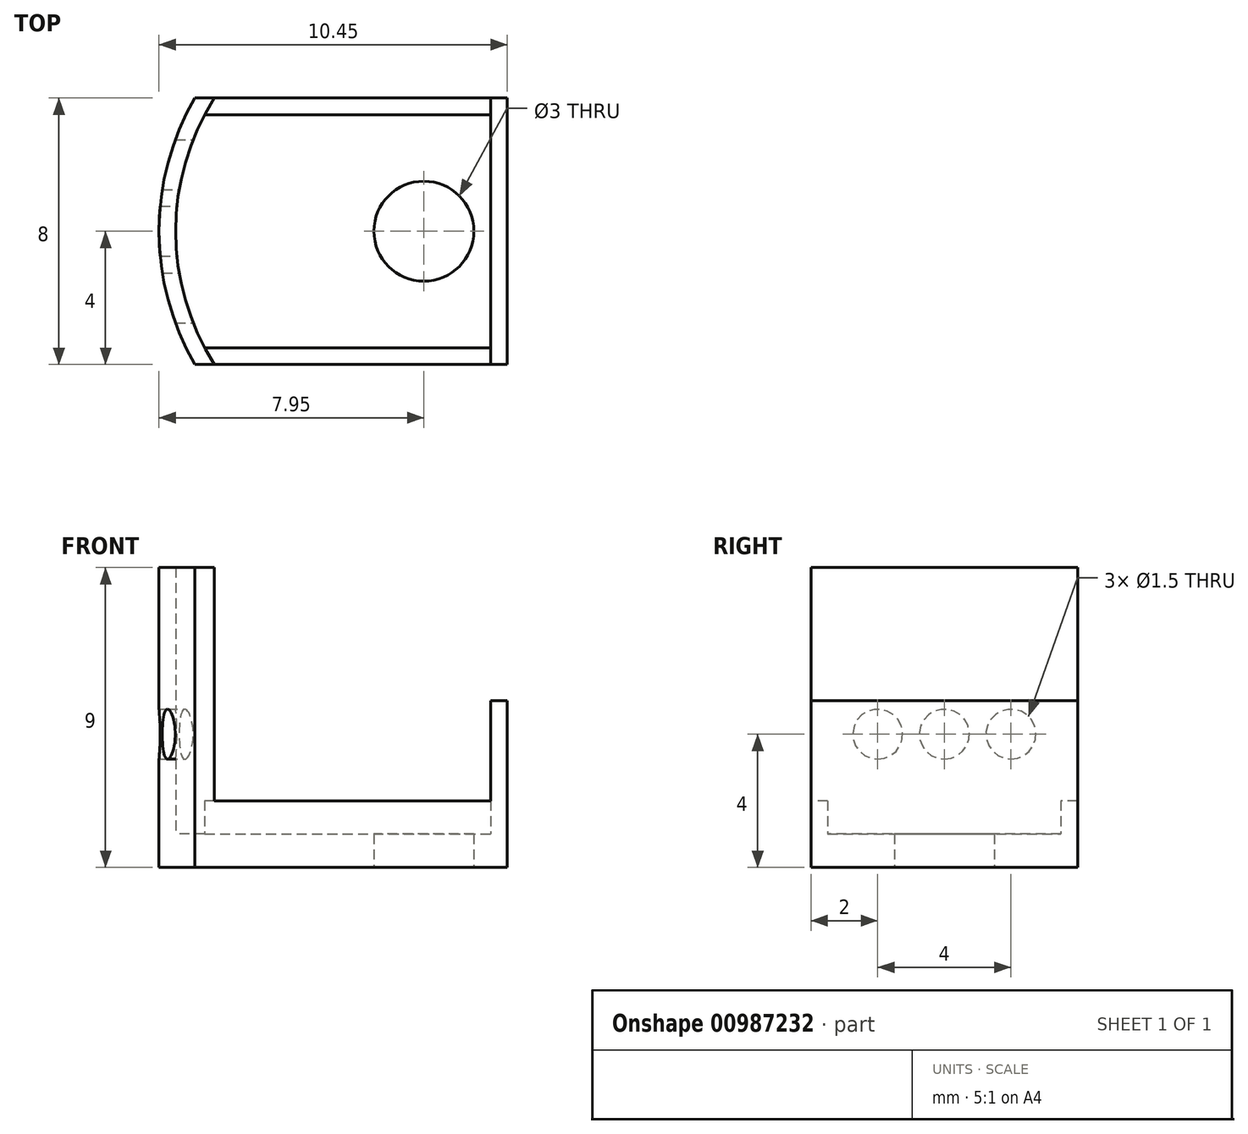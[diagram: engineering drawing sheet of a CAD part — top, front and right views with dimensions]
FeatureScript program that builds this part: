
annotation { "Feature Type Name" : "Feature", "Feature Type Description" : "" }
export const myFeature = defineFeature(function(context is Context, id is Id, definition is map)
    precondition{}
    {
        {
            var Q0;
            Q0=qCreatedBy(makeId("Top.planeOp"),FACE);
            var sketch = newSketch(context, id + "F0", { "sketchPlane" : qUnion([Q0])});
            skLineSegment(sketch, "E0", {"start": v(0, 0) * mm, "end": v(2.5, 0) * mm});
            skCircle(sketch, "E1", {"center": v(0, 0) * mm, "radius": 7.95 * mm});
            skLineSegment(sketch, "E2", {"start": v(2.5, 4) * mm, "end": v(2.5, -4) * mm});
            skLineSegment(sketch, "E3", {"start": v(2.5, 4) * mm, "end": v(-6.87, 4) * mm});
            skCircle(sketch, "E4", {"center": v(0, 0) * mm, "radius": 1.5 * mm});
            skLineSegment(sketch, "E5", {"start": v(2.5, -4) * mm, "end": v(-6.87, -4) * mm});
            skLineSegment(sketch, "E6", {"start": v(2, 4) * mm, "end": v(2, -4) * mm});
            skLineSegment(sketch, "E7", {"start": v(2.5, -3.5) * mm, "end": v(-7.14, -3.5) * mm});
            skLineSegment(sketch, "E8", {"start": v(2.5, 3.5) * mm, "end": v(-7.14, 3.5) * mm});
            skCircle(sketch, "E9", {"center": v(0, 0) * mm, "radius": 7.45 * mm});
            skSolve(sketch);
        }
        {
            var Q0;
            {var subQ5=sQuery(id+"F0.wireOp",EDGE,"E4");Q0=makeQuery(id+"F0.imprint","IMPRINT",FACE,{"disambiguationData":[TD([[makeQuery(id+"F0.imprint","IMPRINT",EDGE,{"derivedFrom":subQ5}),-1.0]])]});}
            var Q1;
            {var subQ0=sQuery(id+"F0.wireOp",EDGE,"E2");var subQ1=sQuery(id+"F0.wireOp",EDGE,"E0");var subQ2=makeQuery(id+"F0.imprint","INTERSECT",VERTEX,{"derivedFrom":[subQ1,subQ0]});Q1=makeQuery(id+"F0.imprint","IMPRINT",FACE,{"disambiguationData":[TD([[makeQuery(id+"F0.imprint","IMPRINT",EDGE,{"disambiguationData":[TD([[subQ2,-1.0]])],"derivedFrom":subQ0}),-1.0]])]});}
            var Q2;
            {var subQ0=sQuery(id+"F0.wireOp",EDGE,"E2");var subQ1=sQuery(id+"F0.wireOp",EDGE,"E0");var subQ2=makeQuery(id+"F0.imprint","INTERSECT",VERTEX,{"derivedFrom":[subQ1,subQ0]});Q2=makeQuery(id+"F0.imprint","IMPRINT",FACE,{"disambiguationData":[TD([[makeQuery(id+"F0.imprint","IMPRINT",EDGE,{"disambiguationData":[TD([[subQ2,1.0]])],"derivedFrom":subQ0}),-1.0]])]});}
            var Q3;
            {var subQ0=sQuery(id+"F0.wireOp",EDGE,"E5");var subQ1=sQuery(id+"F0.wireOp",EDGE,"E1");var subQ2=makeQuery(id+"F0.imprint","INTERSECT",VERTEX,{"derivedFrom":[subQ1,subQ0]});Q3=makeQuery(id+"F0.imprint","IMPRINT",FACE,{"disambiguationData":[TD([[makeQuery(id+"F0.imprint","IMPRINT",EDGE,{"disambiguationData":[TD([[subQ2,1.0]])],"derivedFrom":subQ1}),1.0]])]});}
            var Q4;
            {var subQ0=sQuery(id+"F0.wireOp",EDGE,"E3");var subQ1=sQuery(id+"F0.wireOp",EDGE,"E1");var subQ2=makeQuery(id+"F0.imprint","INTERSECT",VERTEX,{"derivedFrom":[subQ1,subQ0]});Q4=makeQuery(id+"F0.imprint","IMPRINT",FACE,{"disambiguationData":[TD([[makeQuery(id+"F0.imprint","IMPRINT",EDGE,{"disambiguationData":[TD([[subQ2,-1.0]])],"derivedFrom":subQ1}),1.0]])]});}
            var Q5;
            {var subQ0=sQuery(id+"F0.wireOp",EDGE,"E3");var subQ1=sQuery(id+"F0.wireOp",EDGE,"E2");var subQ2=makeQuery(id+"F0.imprint","INTERSECT",VERTEX,{"derivedFrom":[subQ1,subQ0]});Q5=makeQuery(id+"F0.imprint","IMPRINT",FACE,{"disambiguationData":[TD([[makeQuery(id+"F0.imprint","IMPRINT",EDGE,{"disambiguationData":[TD([[subQ2,-1.0]])],"derivedFrom":subQ1}),-1.0]])]});}
            var Q6;
            {var subQ0=sQuery(id+"F0.wireOp",EDGE,"E5");var subQ1=sQuery(id+"F0.wireOp",EDGE,"E2");var subQ2=makeQuery(id+"F0.imprint","INTERSECT",VERTEX,{"derivedFrom":[subQ1,subQ0]});Q6=makeQuery(id+"F0.imprint","IMPRINT",FACE,{"disambiguationData":[TD([[makeQuery(id+"F0.imprint","IMPRINT",EDGE,{"disambiguationData":[TD([[subQ2,1.0]])],"derivedFrom":subQ1}),-1.0]])]});}
            var Q7;
            {var subQ0=sQuery(id+"F0.wireOp",EDGE,"E7");var subQ1=sQuery(id+"F0.wireOp",EDGE,"E1");var subQ2=makeQuery(id+"F0.imprint","INTERSECT",VERTEX,{"derivedFrom":[subQ1,subQ0]});Q7=makeQuery(id+"F0.imprint","IMPRINT",FACE,{"disambiguationData":[TD([[makeQuery(id+"F0.imprint","IMPRINT",EDGE,{"disambiguationData":[TD([[subQ2,1.0]])],"derivedFrom":subQ1}),1.0]])]});}
            var Q8;
            {var subQ0=sQuery(id+"F0.wireOp",EDGE,"E6");var subQ1=sQuery(id+"F0.wireOp",EDGE,"E3");var subQ2=makeQuery(id+"F0.imprint","INTERSECT",VERTEX,{"derivedFrom":[subQ1,subQ0]});Q8=makeQuery(id+"F0.imprint","IMPRINT",FACE,{"disambiguationData":[TD([[makeQuery(id+"F0.imprint","IMPRINT",EDGE,{"disambiguationData":[TD([[subQ2,-1.0]])],"derivedFrom":subQ1}),1.0]])]});}
            var Q9;
            {var subQ0=sQuery(id+"F0.wireOp",EDGE,"E6");var subQ1=sQuery(id+"F0.wireOp",EDGE,"E5");var subQ2=makeQuery(id+"F0.imprint","INTERSECT",VERTEX,{"derivedFrom":[subQ1,subQ0]});Q9=makeQuery(id+"F0.imprint","IMPRINT",FACE,{"disambiguationData":[TD([[makeQuery(id+"F0.imprint","IMPRINT",EDGE,{"disambiguationData":[TD([[subQ2,-1.0]])],"derivedFrom":subQ1}),-1.0]])]});}
            extrude(context, id + "F1", {"entities" : qUnion([Q0, Q1, Q2, Q3, Q4, Q5, Q6, Q7, Q8, Q9]), "depth" : 1 * mm, "offsetDistance" : 25 * mm});
        }
        {
            var Q0;
            {var subQ0=sQuery(id+"F0.wireOp",EDGE,"E2");var subQ1=sQuery(id+"F0.wireOp",EDGE,"E0");var subQ2=makeQuery(id+"F0.imprint","INTERSECT",VERTEX,{"derivedFrom":[subQ1,subQ0]});Q0=makeQuery(id+"F0.imprint","IMPRINT",FACE,{"disambiguationData":[TD([[makeQuery(id+"F0.imprint","IMPRINT",EDGE,{"disambiguationData":[TD([[subQ2,-1.0]])],"derivedFrom":subQ0}),-1.0]])]});}
            var Q1;
            {var subQ0=sQuery(id+"F0.wireOp",EDGE,"E2");var subQ1=sQuery(id+"F0.wireOp",EDGE,"E0");var subQ2=makeQuery(id+"F0.imprint","INTERSECT",VERTEX,{"derivedFrom":[subQ1,subQ0]});Q1=makeQuery(id+"F0.imprint","IMPRINT",FACE,{"disambiguationData":[TD([[makeQuery(id+"F0.imprint","IMPRINT",EDGE,{"disambiguationData":[TD([[subQ2,1.0]])],"derivedFrom":subQ0}),-1.0]])]});}
            var Q2;
            {var subQ0=sQuery(id+"F0.wireOp",EDGE,"E5");var subQ1=sQuery(id+"F0.wireOp",EDGE,"E1");var subQ2=makeQuery(id+"F0.imprint","INTERSECT",VERTEX,{"derivedFrom":[subQ1,subQ0]});Q2=makeQuery(id+"F0.imprint","IMPRINT",FACE,{"disambiguationData":[TD([[makeQuery(id+"F0.imprint","IMPRINT",EDGE,{"disambiguationData":[TD([[subQ2,1.0]])],"derivedFrom":subQ1}),1.0]])]});}
            var Q3;
            {var subQ0=sQuery(id+"F0.wireOp",EDGE,"E5");var subQ1=sQuery(id+"F0.wireOp",EDGE,"E2");var subQ2=makeQuery(id+"F0.imprint","INTERSECT",VERTEX,{"derivedFrom":[subQ1,subQ0]});Q3=makeQuery(id+"F0.imprint","IMPRINT",FACE,{"disambiguationData":[TD([[makeQuery(id+"F0.imprint","IMPRINT",EDGE,{"disambiguationData":[TD([[subQ2,1.0]])],"derivedFrom":subQ1}),-1.0]])]});}
            var Q4;
            {var subQ0=sQuery(id+"F0.wireOp",EDGE,"E3");var subQ1=sQuery(id+"F0.wireOp",EDGE,"E2");var subQ2=makeQuery(id+"F0.imprint","INTERSECT",VERTEX,{"derivedFrom":[subQ1,subQ0]});Q4=makeQuery(id+"F0.imprint","IMPRINT",FACE,{"disambiguationData":[TD([[makeQuery(id+"F0.imprint","IMPRINT",EDGE,{"disambiguationData":[TD([[subQ2,-1.0]])],"derivedFrom":subQ1}),-1.0]])]});}
            var Q5;
            {var subQ0=sQuery(id+"F0.wireOp",EDGE,"E3");var subQ1=sQuery(id+"F0.wireOp",EDGE,"E1");var subQ2=makeQuery(id+"F0.imprint","INTERSECT",VERTEX,{"derivedFrom":[subQ1,subQ0]});Q5=makeQuery(id+"F0.imprint","IMPRINT",FACE,{"disambiguationData":[TD([[makeQuery(id+"F0.imprint","IMPRINT",EDGE,{"disambiguationData":[TD([[subQ2,-1.0]])],"derivedFrom":subQ1}),1.0]])]});}
            var Q6;
            {var subQ0=sQuery(id+"F0.wireOp",EDGE,"E7");var subQ1=sQuery(id+"F0.wireOp",EDGE,"E1");var subQ2=makeQuery(id+"F0.imprint","INTERSECT",VERTEX,{"derivedFrom":[subQ1,subQ0]});Q6=makeQuery(id+"F0.imprint","IMPRINT",FACE,{"disambiguationData":[TD([[makeQuery(id+"F0.imprint","IMPRINT",EDGE,{"disambiguationData":[TD([[subQ2,1.0]])],"derivedFrom":subQ1}),1.0]])]});}
            extrude(context, id + "F2", {"entities" : qUnion([Q0, Q1, Q2, Q3, Q4, Q5, Q6]), "operationType" : NewBodyOperationType.ADD, "depth" : 5 * mm, "offsetDistance" : 25 * mm});
        }
        {
            var Q0;
            {var subQ0=sQuery(id+"F0.wireOp",EDGE,"E6");var subQ1=sQuery(id+"F0.wireOp",EDGE,"E5");var subQ2=makeQuery(id+"F0.imprint","INTERSECT",VERTEX,{"derivedFrom":[subQ1,subQ0]});Q0=makeQuery(id+"F0.imprint","IMPRINT",FACE,{"disambiguationData":[TD([[makeQuery(id+"F0.imprint","IMPRINT",EDGE,{"disambiguationData":[TD([[subQ2,-1.0]])],"derivedFrom":subQ1}),-1.0]])]});}
            var Q1;
            {var subQ0=sQuery(id+"F0.wireOp",EDGE,"E6");var subQ1=sQuery(id+"F0.wireOp",EDGE,"E3");var subQ2=makeQuery(id+"F0.imprint","INTERSECT",VERTEX,{"derivedFrom":[subQ1,subQ0]});Q1=makeQuery(id+"F0.imprint","IMPRINT",FACE,{"disambiguationData":[TD([[makeQuery(id+"F0.imprint","IMPRINT",EDGE,{"disambiguationData":[TD([[subQ2,-1.0]])],"derivedFrom":subQ1}),1.0]])]});}
            extrude(context, id + "F3", {"entities" : qUnion([Q0, Q1]), "operationType" : NewBodyOperationType.ADD, "depth" : 2 * mm, "offsetDistance" : 25 * mm});
        }
        {
            var Q0;
            Q0=makeQuery(id+"F2.opExtrude","CAP_FACE",FACE,{"disambiguationData":[OSD([sQuery(id+"F0.wireOp",EDGE,"E1"),sQuery(id+"F0.wireOp",EDGE,"E3"),sQuery(id+"F0.wireOp",EDGE,"E5"),sQuery(id+"F0.wireOp",EDGE,"E9")])],"isStart":false});
            extrude(context, id + "F4", {"entities" : qUnion([Q0]), "operationType" : NewBodyOperationType.ADD, "depth" : 4 * mm, "offsetDistance" : 25 * mm});
        }
        {
            var Q0;
            Q0=qCreatedBy(makeId("Right.planeOp"),FACE);
            var sketch = newSketch(context, id + "F5", { "sketchPlane" : qUnion([Q0])});
            skLineSegment(sketch, "E10", {"start": v(0, 0) * mm, "end": v(0, 4) * mm});
            skLineSegment(sketch, "E11", {"start": v(0, 4) * mm, "end": v(2, 4) * mm});
            skLineSegment(sketch, "E12", {"start": v(0, 4) * mm, "end": v(-2, 4) * mm});
            skCircle(sketch, "E13", {"center": v(2, 4) * mm, "radius": 0.75 * mm});
            skCircle(sketch, "E14", {"center": v(0, 4) * mm, "radius": 0.75 * mm});
            skCircle(sketch, "E15", {"center": v(-2, 4) * mm, "radius": 0.75 * mm});
            skLineSegment(sketch, "E16", {"start": v(0, 4) * mm, "end": v(0, 5.75) * mm});
            skLineSegment(sketch, "E17", {"start": v(2.23, 5.75) * mm, "end": v(-2.43, 5.75) * mm});
            skCircle(sketch, "E18.MirrorC", {"center": v(2, 7.5) * mm, "radius": 0.75 * mm});
            skCircle(sketch, "E19.MirrorC", {"center": v(0, 7.5) * mm, "radius": 0.75 * mm});
            skCircle(sketch, "E20.MirrorC", {"center": v(-2, 7.5) * mm, "radius": 0.75 * mm});
            skSolve(sketch);
        }
        {
            var Q0;
            Q0=makeQuery(id+"F5.imprint","IMPRINT",FACE,{"disambiguationData":[TD([[makeQuery(id+"F5.imprint","IMPRINT",EDGE,{"derivedFrom":sQuery(id+"F5.wireOp",EDGE,"E13")}),1.0]])]});
            var Q1;
            {var subQ1=sQuery(id+"F5.wireOp",EDGE,"E10");var subQ3=sQuery(id+"F5.wireOp",EDGE,"E14");var subQ4=makeQuery(id+"F5.imprint","INTERSECT",VERTEX,{"derivedFrom":[subQ1,subQ3]});Q1=makeQuery(id+"F5.imprint","IMPRINT",FACE,{"disambiguationData":[TD([[makeQuery(id+"F5.imprint","IMPRINT",EDGE,{"disambiguationData":[TD([[subQ4,-1.0]])],"derivedFrom":subQ3}),1.0]])]});}
            var Q2;
            {var subQ1=sQuery(id+"F5.wireOp",EDGE,"E11");var subQ3=sQuery(id+"F5.wireOp",EDGE,"E14");var subQ4=makeQuery(id+"F5.imprint","INTERSECT",VERTEX,{"derivedFrom":[subQ1,subQ3]});Q2=makeQuery(id+"F5.imprint","IMPRINT",FACE,{"disambiguationData":[TD([[makeQuery(id+"F5.imprint","IMPRINT",EDGE,{"disambiguationData":[TD([[subQ4,-1.0]])],"derivedFrom":subQ3}),1.0]])]});}
            var Q3;
            {var subQ1=sQuery(id+"F5.wireOp",EDGE,"E10");var subQ3=sQuery(id+"F5.wireOp",EDGE,"E14");var subQ4=makeQuery(id+"F5.imprint","INTERSECT",VERTEX,{"derivedFrom":[subQ1,subQ3]});Q3=makeQuery(id+"F5.imprint","IMPRINT",FACE,{"disambiguationData":[TD([[makeQuery(id+"F5.imprint","IMPRINT",EDGE,{"disambiguationData":[TD([[subQ4,1.0]])],"derivedFrom":subQ3}),1.0]])]});}
            var Q4;
            Q4=makeQuery(id+"F5.imprint","IMPRINT",FACE,{"disambiguationData":[TD([[makeQuery(id+"F5.imprint","IMPRINT",EDGE,{"derivedFrom":sQuery(id+"F5.wireOp",EDGE,"E15")}),1.0]])]});
            var Q5;
            {var subQ1=sQuery(id+"F5.wireOp",EDGE,"E12");var subQ3=sQuery(id+"F5.wireOp",EDGE,"E14");var subQ4=makeQuery(id+"F5.imprint","INTERSECT",VERTEX,{"derivedFrom":[subQ1,subQ3]});Q5=makeQuery(id+"F5.imprint","IMPRINT",FACE,{"disambiguationData":[TD([[makeQuery(id+"F5.imprint","IMPRINT",EDGE,{"disambiguationData":[TD([[subQ4,1.0]])],"derivedFrom":subQ3}),1.0]])]});}
            var Q6;
            Q6=makeQuery(id+"F5.imprint","IMPRINT",FACE,{"disambiguationData":[TD([[makeQuery(id+"F5.imprint","IMPRINT",EDGE,{"derivedFrom":sQuery(id+"F5.wireOp",EDGE,"E18.MirrorC")}),-1.0]])]});
            var Q7;
            Q7=makeQuery(id+"F5.imprint","IMPRINT",FACE,{"disambiguationData":[TD([[makeQuery(id+"F5.imprint","IMPRINT",EDGE,{"derivedFrom":sQuery(id+"F5.wireOp",EDGE,"E19.MirrorC")}),-1.0]])]});
            var Q8;
            Q8=makeQuery(id+"F5.imprint","IMPRINT",FACE,{"disambiguationData":[TD([[makeQuery(id+"F5.imprint","IMPRINT",EDGE,{"derivedFrom":sQuery(id+"F5.wireOp",EDGE,"E20.MirrorC")}),-1.0]])]});
            extrude(context, id + "F6", {"entities" : qUnion([Q0, Q1, Q2, Q3, Q4, Q5, Q6, Q7, Q8]), "operationType" : NewBodyOperationType.REMOVE, "oppositeDirection" : true, "depth" : 25 * mm, "offsetDistance" : 25 * mm});
        }
    });
